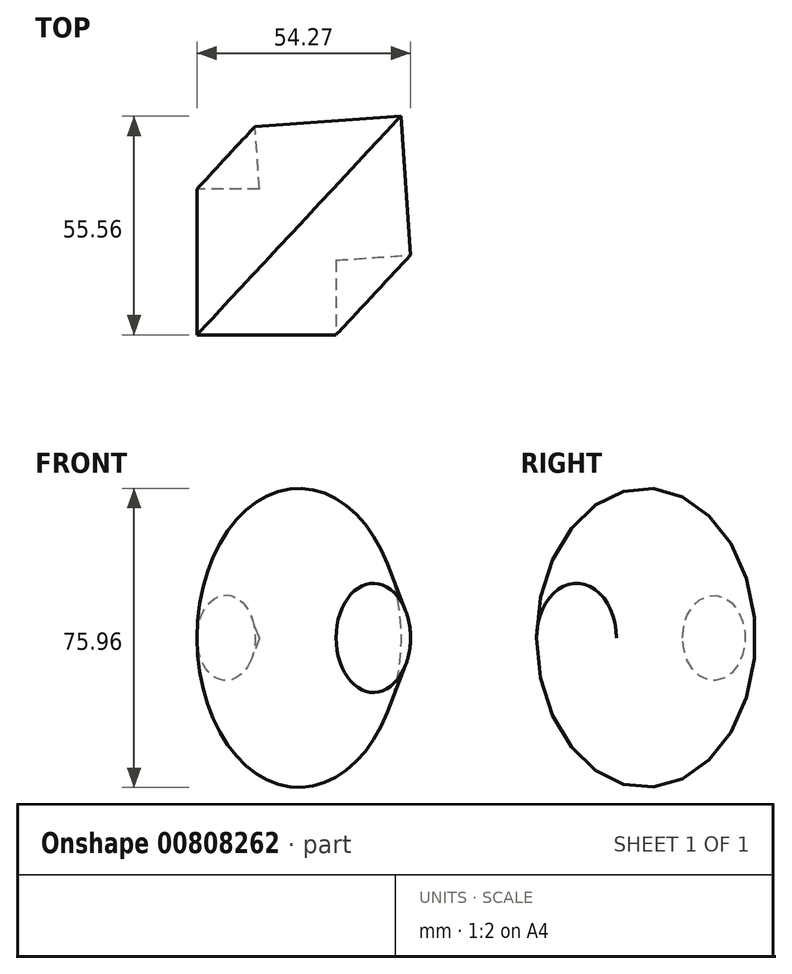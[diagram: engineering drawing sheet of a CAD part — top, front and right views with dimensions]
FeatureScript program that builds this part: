
annotation { "Feature Type Name" : "Feature", "Feature Type Description" : "" }
export const myFeature = defineFeature(function(context is Context, id is Id, definition is map)
    precondition{}
    {
        {
            var Q0;
            Q0=qCreatedBy(makeId("Top.planeOp"),FACE);
            var sketch = newSketch(context, id + "F0", { "sketchPlane" : qUnion([Q0])});
            skLineSegment(sketch, "E0.bottom", {"start": v(-14.57, 20.58) * mm, "end": v(20.78, 20.58) * mm});
            skLineSegment(sketch, "E0.top", {"start": v(-14.57, -16.5) * mm, "end": v(20.78, -16.5) * mm});
            skLineSegment(sketch, "E0.left", {"start": v(-14.57, 20.58) * mm, "end": v(-14.57, -16.5) * mm});
            skLineSegment(sketch, "E0.right", {"start": v(20.78, 20.58) * mm, "end": v(20.78, -16.5) * mm});
            skLineSegment(sketch, "E1", {"start": v(0, 21.82) * mm, "end": v(23.42, 0) * mm});
            skSolve(sketch);
        }
        {
            var Q0;
            {var subQ1=sQuery(id+"F0.wireOp",EDGE,"E0.top");Q0=makeQuery(id+"F0.imprint","IMPRINT",FACE,{"disambiguationData":[TD([[makeQuery(id+"F0.imprint","IMPRINT",EDGE,{"derivedFrom":subQ1}),1.0]])]});}
            var Q1;
            Q1=sQuery(id+"F0.wireOp",EDGE,"E1");
            revolve(context, id + "F1", {"surfaceOperationType" : NewSurfaceOperationType.NEW, "entities" : qUnion([Q0]), "axis" : qUnion([Q1]), "revolveType" : RevolveType.FULL});
        }
    });
